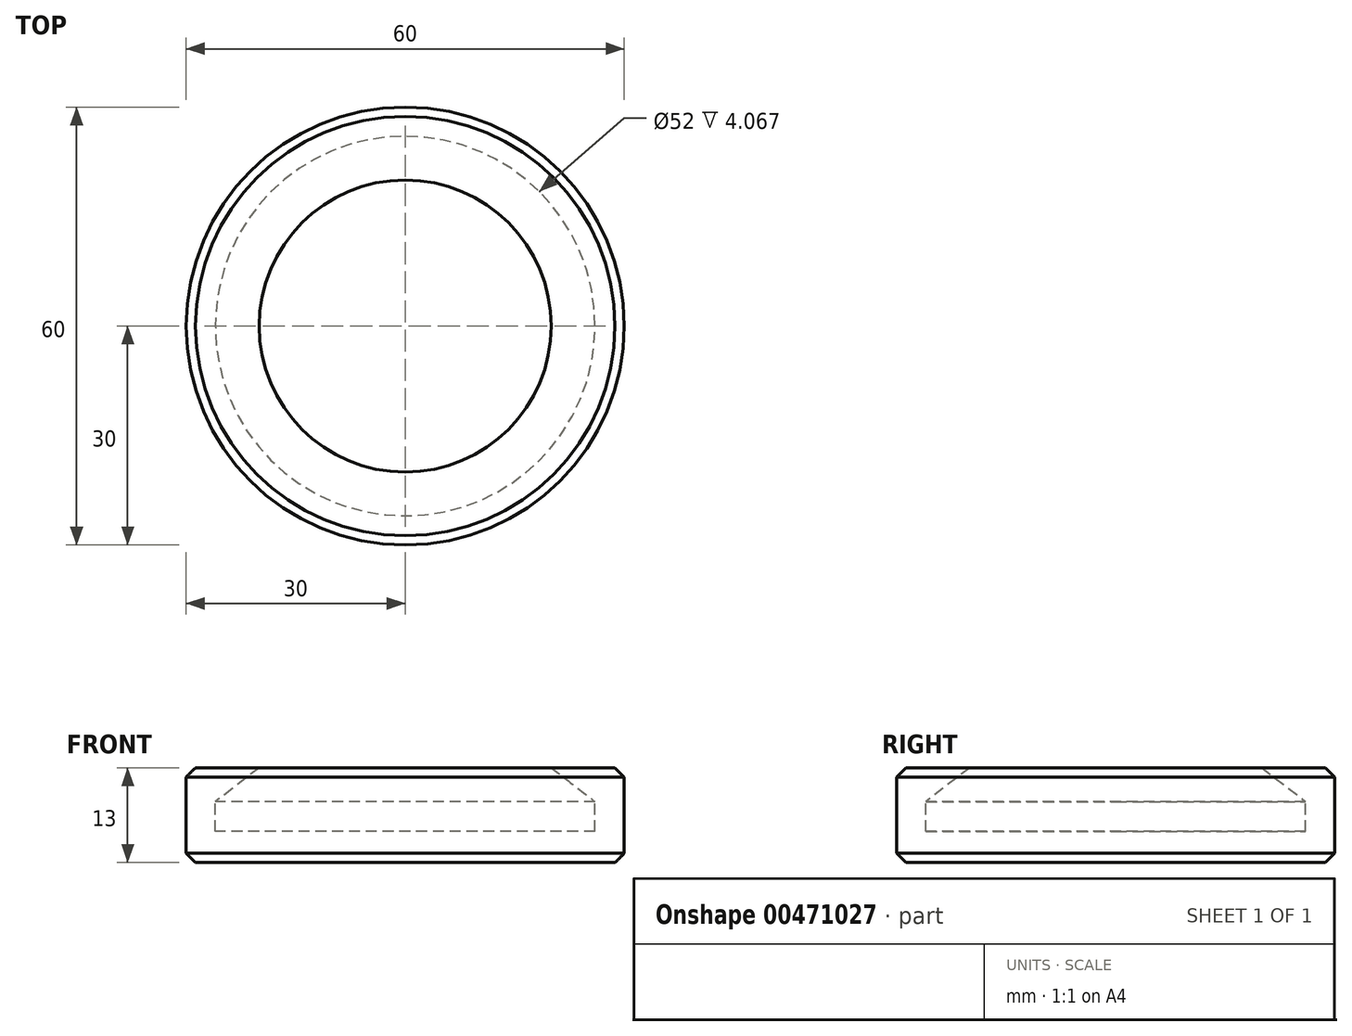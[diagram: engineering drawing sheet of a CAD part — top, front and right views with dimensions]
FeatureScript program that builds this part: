
annotation { "Feature Type Name" : "Feature", "Feature Type Description" : "" }
export const myFeature = defineFeature(function(context is Context, id is Id, definition is map)
    precondition{}
    {
        {
            var Q0;
            Q0=qCreatedBy(makeId("Front.planeOp"),FACE);
            var sketch = newSketch(context, id + "F0", { "sketchPlane" : qUnion([Q0])});
            skLineSegment(sketch, "E0", {"start": v(0, 0) * mm, "end": v(-30, 0) * mm});
            skLineSegment(sketch, "E1", {"start": v(-30, 0) * mm, "end": v(-30, 13) * mm});
            skLineSegment(sketch, "E2", {"start": v(-30, 13) * mm, "end": v(-20, 13) * mm});
            skLineSegment(sketch, "E3", {"start": v(-20, 13) * mm, "end": v(-20, 13) * mm});
            skLineSegment(sketch, "E4", {"start": v(-20, 13) * mm, "end": v(-26, 8.36) * mm});
            skLineSegment(sketch, "E5", {"start": v(-26, 8.36) * mm, "end": v(-26, 4.3) * mm});
            skLineSegment(sketch, "E6", {"start": v(-26, 4.3) * mm, "end": v(0, 4.3) * mm});
            skLineSegment(sketch, "E7", {"start": v(0, 4.3) * mm, "end": v(0, 0) * mm});
            skSolve(sketch);
        }
        {
            var Q0;
            Q0=makeQuery(id+"F0.imprint","IMPRINT",FACE,{"disambiguationData":[TD([[makeQuery(id+"F0.imprint","IMPRINT",EDGE,{"derivedFrom":sQuery(id+"F0.wireOp",EDGE,"E0")}),-1.0]])]});
            var Q1;
            Q1=sQuery(id+"F0.wireOp",EDGE,"E7");
            revolve(context, id + "F1", {"entities" : qUnion([Q0]), "axis" : qUnion([Q1]), "revolveType" : RevolveType.FULL});
        }
        {
            var Q0;
            Q0=makeQuery(id+"F1.opRevolve","SWEPT_EDGE",EDGE,{"disambiguationData":[OSD([sQuery(id+"F0.wireOp",EDGE,"E1"),sQuery(id+"F0.wireOp",EDGE,"E2")])]});
            chamfer(context, id + "F2", {"entities" : qUnion([Q0]), "width" : 1.27 * mm, "tangentPropagation" : true});
        }
        {
            var Q0;
            Q0=makeQuery(id+"F1.opRevolve","SWEPT_EDGE",EDGE,{"disambiguationData":[OSD([sQuery(id+"F0.wireOp",EDGE,"E0"),sQuery(id+"F0.wireOp",EDGE,"E1")])]});
            chamfer(context, id + "F3", {"entities" : qUnion([Q0]), "width" : 1.27 * mm, "tangentPropagation" : true});
        }
    });
